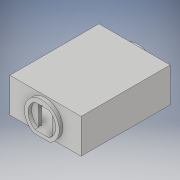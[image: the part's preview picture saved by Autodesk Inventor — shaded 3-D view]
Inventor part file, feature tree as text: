
AUTODESK INVENTOR PART (.ipt)
format: ipt  version: 2017 (Build 210142000, 142)  size: 273,408 bytes
history: native  units: in
note: dims shown in document units (in); Inventor stores cm internally (conversion verified against a paired STEP export)
features: extrude x9, sketch x7, mirror x3, other x1
ambient origin geometry x8: Origin, YZ Plane, XZ Plane, XY Plane, X Axis, Y Axis, Z Axis, Center Point
bodies: Solid1 (feature_tree), Solid2 (feature_tree)
feature tree (20):
  extrude  "floor"  Depth=25.0in
  extrude  "walls"  Depth=1.0in
  extrude  "doorframe"  Depth=1.0in
  extrude  "ceiling"  Depth=8.6667in TaperAngle=0.0deg
  extrude  "left door slot"  Depth=6.6667in
  mirror  "mirror door slot"
  mirror  "right door slot"
  sketch  "Sketch10"  dims[d20=8.6667in d21=0.0in d22=1.0in d23=0.0in]
  extrude  "corridor connect"  Depth=1.0in TaperAngle=0.0deg
  sketch  "Sketch11"  dims[d24=0.25in d25=0.5in d26=2.0in d27=0.0in d28=6.6667in d37=6.6667in d38=4.0in d39=1.0in d40=1.0in d41=0.0in d42=0.5833in d43=0.0625in d44=0.0625in d45=0.125in d46=0.25in d47=0.125in d48=45.0deg d49=0.0892in d50=0.0884in d51=1.0in d52=0.0in d53=1.0in d54=0.0in d55=1.0in d56=0.0in]
  extrude  "light"  Depth=0.5in
  extrude  "into wall light cut"  Depth=2.0in TaperAngle=0.0deg
  extrude  "into wall light join"  Depth=6.6667in
  other  "middle of the room"
  mirror  "Mirror connection for starting door"
  sketch  "Sketch1"  dims[d0=20.0in d1=25.0in]
  sketch  "Sketch4"  dims[d2=1.0in d3=0.0in d11=1.0in]
  sketch  "Sketch5"  dims[d12=1.0in d13=1.0in]
  sketch  "Sketch7"  dims[d14=1.0in d15=8.6667in d16=0.0in]
  sketch  "Sketch8"  dims[d17=2.0in d18=6.6667in]
